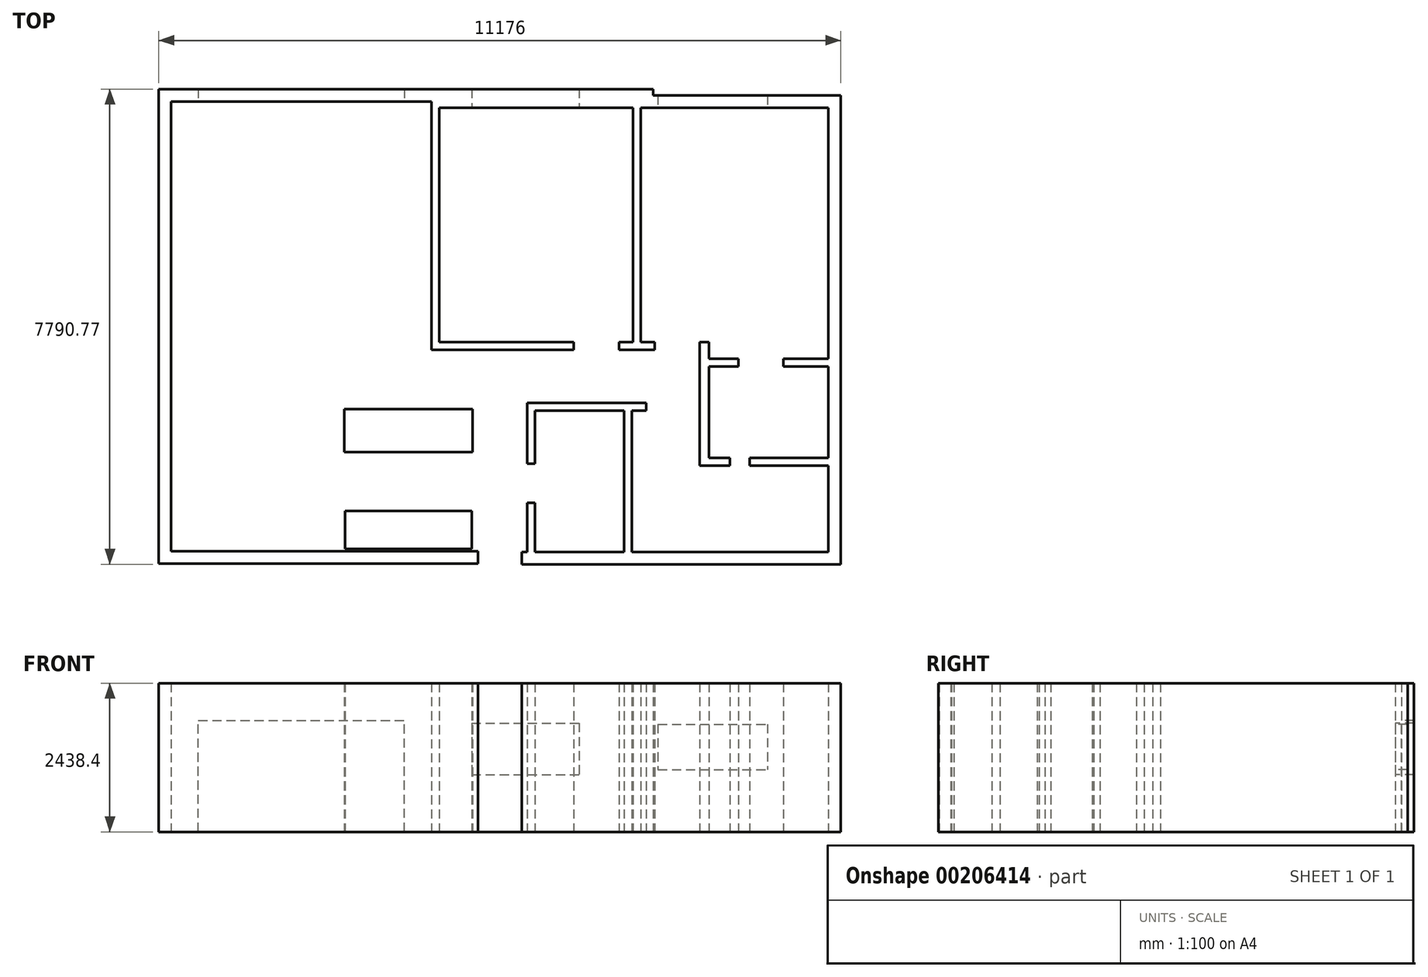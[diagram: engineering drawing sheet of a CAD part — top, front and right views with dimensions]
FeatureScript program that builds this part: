
annotation { "Feature Type Name" : "Feature", "Feature Type Description" : "" }
export const myFeature = defineFeature(function(context is Context, id is Id, definition is map)
    precondition{}
    {
        {
            var Q0;
            Q0=qCreatedBy(makeId("Top.planeOp"),FACE);
            var sketch = newSketch(context, id + "F0", { "sketchPlane" : qUnion([Q0])});
            skLineSegment(sketch, "E0", {"start": v(-1680.87, -2985) * mm, "end": v(2586.33, -2985) * mm});
            skLineSegment(sketch, "E1", {"start": v(-1680.87, -2985) * mm, "end": v(-1680.87, -10359.28) * mm});
            skLineSegment(sketch, "E2", {"start": v(-1680.87, -10359.28) * mm, "end": v(3344.46, -10359.28) * mm});
            skLineSegment(sketch, "E3", {"start": v(2586.33, -2985) * mm, "end": v(2586.33, -7060.8) * mm});
            skLineSegment(sketch, "E4", {"start": v(2713.33, -3088.6) * mm, "end": v(5888.33, -3088.6) * mm});
            skLineSegment(sketch, "E5", {"start": v(5888.33, -3088.6) * mm, "end": v(5888.33, -6933.8) * mm});
            skLineSegment(sketch, "E6", {"start": v(5888.33, -6933.8) * mm, "end": v(5655.05, -6933.8) * mm});
            skLineSegment(sketch, "E7", {"start": v(4915.79, -6933.8) * mm, "end": v(2713.33, -6933.8) * mm});
            skLineSegment(sketch, "E8", {"start": v(6015.33, -3088.6) * mm, "end": v(6015.33, -6933.31) * mm});
            skLineSegment(sketch, "E9", {"start": v(6015.33, -6933.31) * mm, "end": v(6241.73, -6933.31) * mm});
            skLineSegment(sketch, "E10", {"start": v(4915.79, -6933.8) * mm, "end": v(4915.79, -7060.8) * mm});
            skLineSegment(sketch, "E11", {"start": v(4915.79, -7060.8) * mm, "end": v(2586.33, -7060.8) * mm});
            skLineSegment(sketch, "E12", {"start": v(2713.33, -6933.8) * mm, "end": v(2713.33, -3088.6) * mm});
            skLineSegment(sketch, "E13", {"start": v(-1884.07, -10562.48) * mm, "end": v(-1884.07, -2781.8) * mm});
            skLineSegment(sketch, "E14", {"start": v(-1884.07, -2781.8) * mm, "end": v(6218.53, -2781.8) * mm});
            skLineSegment(sketch, "E15", {"start": v(6218.53, -2781.8) * mm, "end": v(6218.53, -2885.4) * mm});
            skLineSegment(sketch, "E16", {"start": v(6218.53, -2885.4) * mm, "end": v(9291.93, -2885.4) * mm});
            skLineSegment(sketch, "E17", {"start": v(9291.93, -2885.4) * mm, "end": v(9291.93, -10572.58) * mm});
            skLineSegment(sketch, "E18", {"start": v(4067.27, -10369.38) * mm, "end": v(9088.73, -10369.38) * mm});
            skLineSegment(sketch, "E19", {"start": v(9088.73, -10369.38) * mm, "end": v(9088.73, -3088.6) * mm});
            skLineSegment(sketch, "E20", {"start": v(9088.73, -3088.6) * mm, "end": v(6015.33, -3088.6) * mm});
            skLineSegment(sketch, "E21", {"start": v(9291.93, -10572.58) * mm, "end": v(4067.27, -10572.58) * mm});
            skLineSegment(sketch, "E22", {"start": v(4067.27, -10572.58) * mm, "end": v(4067.27, -10369.38) * mm});
            skLineSegment(sketch, "E23", {"start": v(6241.73, -6933.31) * mm, "end": v(6241.73, -7060.8) * mm});
            skLineSegment(sketch, "E24", {"start": v(6241.73, -7060.8) * mm, "end": v(5655.05, -7060.8) * mm});
            skLineSegment(sketch, "E25", {"start": v(5655.05, -7060.8) * mm, "end": v(5655.05, -6933.8) * mm});
            skLineSegment(sketch, "E26", {"start": v(3344.46, -10359.28) * mm, "end": v(3344.46, -10562.48) * mm});
            skLineSegment(sketch, "E27", {"start": v(-1884.07, -10562.48) * mm, "end": v(3344.46, -10562.48) * mm});
            skLineSegment(sketch, "E28", {"start": v(9088.73, -7203.4) * mm, "end": v(8353.5, -7203.4) * mm});
            skLineSegment(sketch, "E29", {"start": v(6981, -6933.31) * mm, "end": v(6981, -7060.31) * mm});
            skLineSegment(sketch, "E30", {"start": v(6981, -6933.31) * mm, "end": v(7130.16, -6933.31) * mm});
            skLineSegment(sketch, "E31", {"start": v(7130.16, -6933.31) * mm, "end": v(7130.16, -7203.4) * mm});
            skLineSegment(sketch, "E32", {"start": v(7130.16, -7203.4) * mm, "end": v(7614.24, -7203.4) * mm});
            skLineSegment(sketch, "E33", {"start": v(7614.24, -7203.4) * mm, "end": v(7614.24, -7330.4) * mm});
            skLineSegment(sketch, "E34", {"start": v(9088.73, -7330.4) * mm, "end": v(8353.5, -7330.4) * mm});
            skLineSegment(sketch, "E35", {"start": v(8353.5, -7330.4) * mm, "end": v(8353.5, -7203.4) * mm});
            skLineSegment(sketch, "E36", {"start": v(7614.24, -7330.4) * mm, "end": v(7130.16, -7330.4) * mm});
            skLineSegment(sketch, "E37", {"start": v(7130.16, -7330.4) * mm, "end": v(7130.16, -8827.83) * mm});
            skLineSegment(sketch, "E38", {"start": v(7130.16, -8827.83) * mm, "end": v(7474.02, -8827.83) * mm});
            skLineSegment(sketch, "E39", {"start": v(7474.02, -8827.83) * mm, "end": v(7474.02, -8954.83) * mm});
            skLineSegment(sketch, "E40", {"start": v(7474.02, -8954.83) * mm, "end": v(6981, -8954.83) * mm});
            skLineSegment(sketch, "E41", {"start": v(6981, -8954.83) * mm, "end": v(6981, -7060.31) * mm});
            skLineSegment(sketch, "E42", {"start": v(7800.38, -8827.83) * mm, "end": v(9088.73, -8827.83) * mm});
            skLineSegment(sketch, "E43", {"start": v(7800.38, -8827.83) * mm, "end": v(7800.38, -8954.83) * mm});
            skLineSegment(sketch, "E44", {"start": v(7800.38, -8954.83) * mm, "end": v(9088.73, -8954.83) * mm});
            skLineSegment(sketch, "E45", {"start": v(4153.7, -10369.38) * mm, "end": v(4153.7, -9563.74) * mm});
            skLineSegment(sketch, "E46", {"start": v(4153.7, -9563.74) * mm, "end": v(4280.7, -9563.74) * mm});
            skLineSegment(sketch, "E47", {"start": v(4280.7, -9563.74) * mm, "end": v(4280.7, -10369.38) * mm});
            skLineSegment(sketch, "E48", {"start": v(4153.7, -8926.12) * mm, "end": v(4153.7, -7928.1) * mm});
            skLineSegment(sketch, "E49", {"start": v(4153.7, -7928.1) * mm, "end": v(6103.62, -7928.1) * mm});
            skLineSegment(sketch, "E50", {"start": v(6103.62, -7928.1) * mm, "end": v(6103.62, -8055.1) * mm});
            skLineSegment(sketch, "E51", {"start": v(6103.62, -8055.1) * mm, "end": v(5868.08, -8055.1) * mm});
            skLineSegment(sketch, "E52", {"start": v(5868.08, -8055.1) * mm, "end": v(5868.08, -10369.38) * mm});
            skLineSegment(sketch, "E53", {"start": v(4280.7, -8926.12) * mm, "end": v(4280.7, -8055.1) * mm});
            skLineSegment(sketch, "E54", {"start": v(4280.7, -8055.1) * mm, "end": v(5741.08, -8055.1) * mm});
            skLineSegment(sketch, "E55", {"start": v(5741.08, -8055.1) * mm, "end": v(5741.08, -10369.38) * mm});
            skLineSegment(sketch, "E56", {"start": v(4153.7, -8926.12) * mm, "end": v(4280.7, -8926.12) * mm});
            skSolve(sketch);
        }
        {
            var Q0;
            Q0 = qSketchRegion(id + "F0", true);
            extrude(context, id + "F1", {"entities" : qUnion([Q0]), "depth" : 2438.4 * mm});
        }
        {
            var Q0;
            Q0=makeQuery(id+"F1.opExtrude","SWEPT_FACE",FACE,{"disambiguationData":[OSD([sQuery(id+"F0.wireOp",EDGE,"E0")])]});
            var sketch = newSketch(context, id + "F2", { "sketchPlane" : qUnion([Q0])});
            skLineSegment(sketch, "E57.bottom", {"start": v(-1235.34, 0) * mm, "end": v(2142.86, 0) * mm});
            skLineSegment(sketch, "E57.top", {"start": v(-1235.34, 1828.8) * mm, "end": v(2142.86, 1828.8) * mm});
            skLineSegment(sketch, "E57.left", {"start": v(-1235.34, 0) * mm, "end": v(-1235.34, 1828.8) * mm});
            skLineSegment(sketch, "E57.right", {"start": v(2142.86, 0) * mm, "end": v(2142.86, 1828.8) * mm});
            skSolve(sketch);
        }
        {
            var Q0;
            Q0=makeQuery(id+"F2.imprint","IMPRINT",FACE,{"disambiguationData":[TD([[makeQuery(id+"F2.imprint","IMPRINT",EDGE,{"derivedFrom":sQuery(id+"F2.wireOp",EDGE,"E57.bottom")}),1.0]])]});
            extrude(context, id + "F3", {"entities" : qUnion([Q0]), "operationType" : NewBodyOperationType.REMOVE, "endBound" : BoundingType.UP_TO_NEXT, "oppositeDirection" : true, "depth" : 25.4 * mm});
        }
        {
            var Q0;
            Q0=makeQuery(id+"F1.opExtrude","SWEPT_FACE",FACE,{"disambiguationData":[OSD([sQuery(id+"F0.wireOp",EDGE,"E4")])]});
            var sketch = newSketch(context, id + "F4", { "sketchPlane" : qUnion([Q0])});
            skLineSegment(sketch, "E58.bottom", {"start": v(3242.57, 1784.88) * mm, "end": v(5006.6, 1784.88) * mm});
            skLineSegment(sketch, "E58.top", {"start": v(3242.57, 940.51) * mm, "end": v(5006.6, 940.51) * mm});
            skLineSegment(sketch, "E58.left", {"start": v(3242.57, 1784.88) * mm, "end": v(3242.57, 940.51) * mm});
            skLineSegment(sketch, "E58.right", {"start": v(5006.6, 1784.88) * mm, "end": v(5006.6, 940.51) * mm});
            skSolve(sketch);
        }
        {
            var Q0;
            Q0=makeQuery(id+"F1.opExtrude","SWEPT_FACE",FACE,{"disambiguationData":[OSD([sQuery(id+"F0.wireOp",EDGE,"E20")])]});
            var sketch = newSketch(context, id + "F5", { "sketchPlane" : qUnion([Q0])});
            skLineSegment(sketch, "E59.bottom", {"start": v(6295.7, 1765.69) * mm, "end": v(8086.87, 1765.69) * mm});
            skLineSegment(sketch, "E59.top", {"start": v(6295.7, 1017.27) * mm, "end": v(8086.87, 1017.27) * mm});
            skLineSegment(sketch, "E59.left", {"start": v(6295.7, 1765.69) * mm, "end": v(6295.7, 1017.27) * mm});
            skLineSegment(sketch, "E59.right", {"start": v(8086.87, 1765.69) * mm, "end": v(8086.87, 1017.27) * mm});
            skSolve(sketch);
        }
        {
            var Q0;
            Q0 = qSketchRegion(id + "F5", true);
            var Q1;
            Q1 = qSketchRegion(id + "F4", true);
            extrude(context, id + "F6", {"entities" : qUnion([Q0, Q1]), "operationType" : NewBodyOperationType.REMOVE, "endBound" : BoundingType.UP_TO_NEXT, "oppositeDirection" : true, "depth" : 25.4 * mm});
        }
        {
            var Q0;
            Q0=qCreatedBy(makeId("Top.planeOp"),FACE);
            var sketch = newSketch(context, id + "F7", { "sketchPlane" : qUnion([Q0])});
            skLineSegment(sketch, "E60.bottom", {"start": v(1152.88, -8029.93) * mm, "end": v(3256.14, -8029.93) * mm});
            skLineSegment(sketch, "E60.top", {"start": v(1152.88, -8735.54) * mm, "end": v(3256.14, -8735.54) * mm});
            skLineSegment(sketch, "E60.left", {"start": v(1152.88, -8029.93) * mm, "end": v(1152.88, -8735.54) * mm});
            skLineSegment(sketch, "E60.right", {"start": v(3256.14, -8029.93) * mm, "end": v(3256.14, -8735.54) * mm});
            skLineSegment(sketch, "E61.bottom", {"start": v(1166.45, -9698.97) * mm, "end": v(3242.57, -9698.97) * mm});
            skLineSegment(sketch, "E61.top", {"start": v(1166.45, -10323.16) * mm, "end": v(3242.57, -10323.16) * mm});
            skLineSegment(sketch, "E61.left", {"start": v(1166.45, -9698.97) * mm, "end": v(1166.45, -10323.16) * mm});
            skLineSegment(sketch, "E61.right", {"start": v(3242.57, -9698.97) * mm, "end": v(3242.57, -10323.16) * mm});
            skSolve(sketch);
        }
        {
            var Q0;
            Q0=makeQuery(id+"F7.imprint","IMPRINT",FACE,{"disambiguationData":[TD([[makeQuery(id+"F7.imprint","IMPRINT",EDGE,{"derivedFrom":sQuery(id+"F7.wireOp",EDGE,"E60.bottom")}),-1.0]])]});
            var Q1;
            Q1=makeQuery(id+"F7.imprint","IMPRINT",FACE,{"disambiguationData":[TD([[makeQuery(id+"F7.imprint","IMPRINT",EDGE,{"derivedFrom":sQuery(id+"F7.wireOp",EDGE,"E61.bottom")}),-1.0]])]});
            extrude(context, id + "F8", {"entities" : qUnion([Q0, Q1]), "depth" : 2438.4 * mm});
        }
    });
